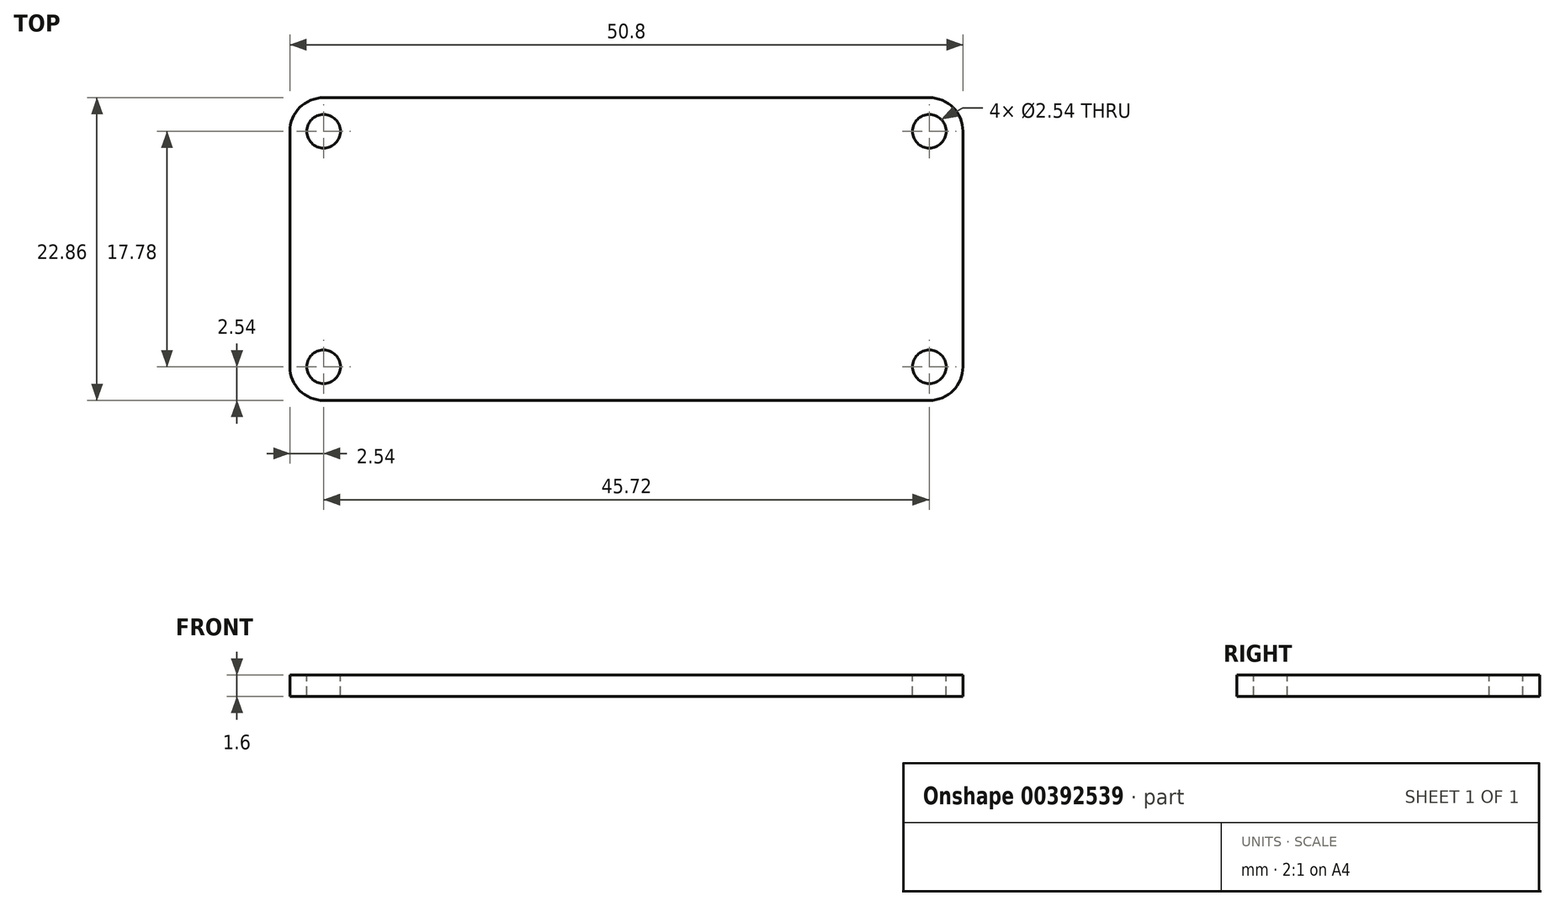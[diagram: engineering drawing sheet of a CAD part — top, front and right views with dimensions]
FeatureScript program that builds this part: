
annotation { "Feature Type Name" : "Feature", "Feature Type Description" : "" }
export const myFeature = defineFeature(function(context is Context, id is Id, definition is map)
    precondition{}
    {
        {
            var Q0;
            Q0=qCreatedBy(makeId("Top.planeOp"),FACE);
            var sketch = newSketch(context, id + "F0", { "sketchPlane" : qUnion([Q0])});
            skLineSegment(sketch, "E0.bottom", {"start": v(-22.86, 11.43) * mm, "end": v(22.86, 11.43) * mm});
            skLineSegment(sketch, "E0.top", {"start": v(-22.86, -11.43) * mm, "end": v(22.86, -11.43) * mm});
            skLineSegment(sketch, "E0.left", {"start": v(-25.4, 8.9) * mm, "end": v(-25.4, -8.89) * mm});
            skLineSegment(sketch, "E0.right", {"start": v(25.4, 8.89) * mm, "end": v(25.4, -8.89) * mm});
            skPoint(sketch, "E1", {"position": v(0, 11.43) * mm});
            skPoint(sketch, "E2", {"position": v(-25.4, 0) * mm});
            skPoint(sketch, "E3.visualSharp", {"position": v(-25.4, 11.43) * mm});
            skArc(sketch, "E3.filletArc", {"start": v(-22.86, 11.43) * mm, "mid": v(-24.66, 10.69) * mm, "end": v(-25.4, 8.9) * mm});
            skPoint(sketch, "E4.visualSharp", {"position": v(-25.4, -11.43) * mm});
            skArc(sketch, "E4.filletArc", {"start": v(-25.4, -8.89) * mm, "mid": v(-24.66, -10.69) * mm, "end": v(-22.86, -11.43) * mm});
            skPoint(sketch, "E5.visualSharp", {"position": v(25.4, -11.43) * mm});
            skArc(sketch, "E5.filletArc", {"start": v(22.86, -11.43) * mm, "mid": v(24.66, -10.69) * mm, "end": v(25.4, -8.89) * mm});
            skPoint(sketch, "E6.visualSharp", {"position": v(25.4, 11.43) * mm});
            skArc(sketch, "E6.filletArc", {"start": v(25.4, 8.89) * mm, "mid": v(24.66, 10.69) * mm, "end": v(22.86, 11.43) * mm});
            skCircle(sketch, "E7", {"center": v(-22.86, 8.9) * mm, "radius": 1.27 * mm});
            skCircle(sketch, "E8", {"center": v(-22.86, -8.89) * mm, "radius": 1.27 * mm});
            skCircle(sketch, "E9", {"center": v(22.86, -8.89) * mm, "radius": 1.27 * mm});
            skCircle(sketch, "E10", {"center": v(22.86, 8.89) * mm, "radius": 1.27 * mm});
            skSolve(sketch);
        }
        {
            var Q0;
            Q0=makeQuery(id+"F0.imprint","IMPRINT",FACE,{"disambiguationData":[TD([[makeQuery(id+"F0.imprint","IMPRINT",EDGE,{"derivedFrom":sQuery(id+"F0.wireOp",EDGE,"E0.bottom")}),-1.0]])]});
            extrude(context, id + "F1", {"entities" : qUnion([Q0]), "oppositeDirection" : true, "depth" : 1.6 * mm});
        }
    });
